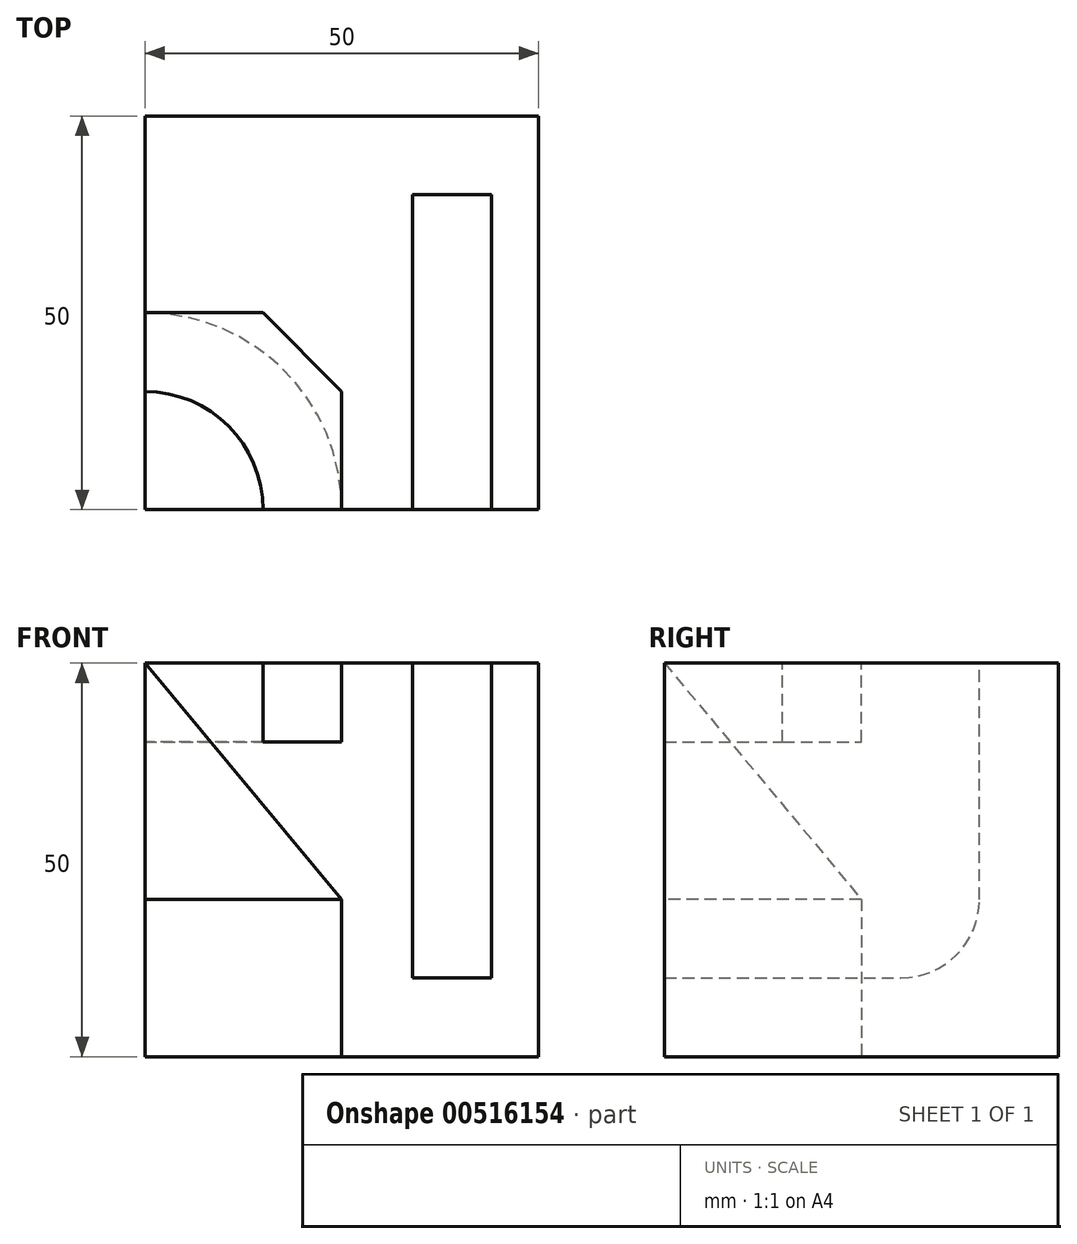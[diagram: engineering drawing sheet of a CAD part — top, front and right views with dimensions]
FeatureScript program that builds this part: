
annotation { "Feature Type Name" : "Feature", "Feature Type Description" : "" }
export const myFeature = defineFeature(function(context is Context, id is Id, definition is map)
    precondition{}
    {
        {
            var Q0;
            Q0=qCreatedBy(makeId("Top.planeOp"),FACE);
            var sketch = newSketch(context, id + "F0", { "sketchPlane" : qUnion([Q0])});
            skLineSegment(sketch, "E0.bottom", {"start": v(0, 0) * mm, "end": v(50, 0) * mm});
            skLineSegment(sketch, "E0.top", {"start": v(0, 50) * mm, "end": v(50, 50) * mm});
            skLineSegment(sketch, "E0.left", {"start": v(0, 0) * mm, "end": v(0, 50) * mm});
            skLineSegment(sketch, "E0.right", {"start": v(50, 0) * mm, "end": v(50, 50) * mm});
            skSolve(sketch);
        }
        {
            var Q0;
            Q0=makeQuery(id+"F0.imprint","IMPRINT",FACE,{"disambiguationData":[TD([[makeQuery(id+"F0.imprint","IMPRINT",EDGE,{"derivedFrom":sQuery(id+"F0.wireOp",EDGE,"E0.bottom")}),1.0]])]});
            extrude(context, id + "F1", {"entities" : qUnion([Q0]), "depth" : 50 * mm, "offsetDistance" : 25 * mm});
        }
        {
            var Q0;
            Q0=makeQuery(id+"F1.opExtrude","CAP_FACE",FACE,{"disambiguationData":[OSD([sQuery(id+"F0.wireOp",EDGE,"E0.bottom"),sQuery(id+"F0.wireOp",EDGE,"E0.top"),sQuery(id+"F0.wireOp",EDGE,"E0.left"),sQuery(id+"F0.wireOp",EDGE,"E0.right")])],"isStart":false});
            var sketch = newSketch(context, id + "F2", { "sketchPlane" : qUnion([Q0])});
            skCircle(sketch, "E1", {"center": v(0, 0) * mm, "radius": 15 * mm});
            skLineSegment(sketch, "E2.bottom", {"start": v(0, 0) * mm, "end": v(25, 0) * mm});
            skLineSegment(sketch, "E2.top", {"start": v(0, 25) * mm, "end": v(25, 25) * mm});
            skLineSegment(sketch, "E2.left", {"start": v(0, 0) * mm, "end": v(0, 25) * mm});
            skLineSegment(sketch, "E2.right", {"start": v(25, 0) * mm, "end": v(25, 25) * mm});
            skLineSegment(sketch, "E3", {"start": v(15, 25) * mm, "end": v(25, 15) * mm});
            skSolve(sketch);
        }
        {
            var Q0;
            {var subQ5=sQuery(id+"F2.wireOp",EDGE,"E3");Q0=makeQuery(id+"F2.imprint","IMPRINT",FACE,{"disambiguationData":[TD([[makeQuery(id+"F2.imprint","IMPRINT",EDGE,{"derivedFrom":subQ5}),-1.0]])]});}
            extrude(context, id + "F3", {"entities" : qUnion([Q0]), "operationType" : NewBodyOperationType.REMOVE, "oppositeDirection" : true, "depth" : 10 * mm, "offsetDistance" : 25 * mm});
        }
        {
            var Q0;
            {var subQ0=sQuery(id+"F0.wireOp",EDGE,"E0.left");var subQ1=sQuery(id+"F0.wireOp",EDGE,"E0.top");var subQ2=sQuery(id+"F0.wireOp",EDGE,"E0.right");var subQ3=sQuery(id+"F0.wireOp",EDGE,"E0.bottom");Q0=makeQuery(id+"F3.boolean.opBoolean","SPLIT",FACE,{"disambiguationData":[TD([makeQuery(id+"F1.opExtrude","SWEPT_FACE",FACE,{"disambiguationData":[OSD([subQ1])]})])],"derivedFrom":makeQuery(id+"F1.opExtrude","CAP_FACE",FACE,{"disambiguationData":[OSD([subQ3,subQ1,subQ0,subQ2])],"isStart":false})});}
            var sketch = newSketch(context, id + "F4", { "sketchPlane" : qUnion([Q0])});
            skLineSegment(sketch, "E4.bottom", {"start": v(34, 0) * mm, "end": v(44, 0) * mm});
            skLineSegment(sketch, "E4.top", {"start": v(34, 40) * mm, "end": v(44, 40) * mm});
            skLineSegment(sketch, "E4.left", {"start": v(34, 0) * mm, "end": v(34, 40) * mm});
            skLineSegment(sketch, "E4.right", {"start": v(44, 0) * mm, "end": v(44, 40) * mm});
            skSolve(sketch);
        }
        {
            var Q0;
            Q0=makeQuery(id+"F4.imprint","IMPRINT",FACE,{"disambiguationData":[TD([[makeQuery(id+"F4.imprint","IMPRINT",EDGE,{"derivedFrom":sQuery(id+"F4.wireOp",EDGE,"E4.bottom")}),1.0]])]});
            extrude(context, id + "F5", {"entities" : qUnion([Q0]), "operationType" : NewBodyOperationType.REMOVE, "oppositeDirection" : true, "depth" : 40 * mm, "offsetDistance" : 25 * mm});
        }
        {
            var Q0;
            Q0=makeQuery(id+"F5.boolean.opBoolean","COPY",EDGE,{"derivedFrom":makeQuery(id+"F5.opExtrude","CAP_EDGE",EDGE,{"disambiguationData":[OSD([sQuery(id+"F4.wireOp",EDGE,"E4.top")])],"isStart":false})});
            fillet(context, id + "F6", {"entities" : qUnion([Q0]), "radius" : 10 * mm, "tangentPropagation" : true, "allowEdgeOverflow" : false});
        }
        {
            var Q0;
            Q0=makeQuery(id+"F1.opExtrude","CAP_FACE",FACE,{"disambiguationData":[OSD([sQuery(id+"F0.wireOp",EDGE,"E0.bottom"),sQuery(id+"F0.wireOp",EDGE,"E0.top"),sQuery(id+"F0.wireOp",EDGE,"E0.left"),sQuery(id+"F0.wireOp",EDGE,"E0.right")])],"isStart":true});
            var sketch = newSketch(context, id + "F7", { "sketchPlane" : qUnion([Q0])});
            skCircle(sketch, "E5", {"center": v(0, 0) * mm, "radius": 25 * mm});
            skSolve(sketch);
        }
        {
            var Q0;
            {var subQ0=sQuery(id+"F7.wireOp",EDGE,"E5");var subQ1=makeQuery(id+"F1.opExtrude","CAP_EDGE",EDGE,{"disambiguationData":[OSD([sQuery(id+"F0.wireOp",EDGE,"E0.bottom")])],"isStart":true});var subQ2=makeQuery(id+"F7.imprint","INTERSECT",VERTEX,{"derivedFrom":[subQ1,subQ0]});Q0=makeQuery(id+"F7.imprint","IMPRINT",FACE,{"disambiguationData":[TD([[makeQuery(id+"F7.imprint","IMPRINT",EDGE,{"disambiguationData":[TD([[subQ2,1.0]])],"derivedFrom":subQ0}),1.0]])]});}
            extrude(context, id + "F8", {"entities" : qUnion([Q0]), "operationType" : NewBodyOperationType.REMOVE, "oppositeDirection" : true, "depth" : 20 * mm, "offsetDistance" : 25 * mm});
        }
        {
            var Q0;
            Q0=makeQuery(id+"F1.opExtrude","SWEPT_FACE",FACE,{"disambiguationData":[OSD([sQuery(id+"F0.wireOp",EDGE,"E0.bottom")])]});
            var sketch = newSketch(context, id + "F9", { "sketchPlane" : qUnion([Q0])});
            skLineSegment(sketch, "E6", {"start": v(25, 20) * mm, "end": v(0, 50) * mm});
            skSolve(sketch);
        }
        {
            var Q0;
            Q0=makeQuery(id+"F9.imprint","IMPRINT",FACE,{"disambiguationData":[TD([[makeQuery(id+"F9.imprint","IMPRINT",EDGE,{"derivedFrom":sQuery(id+"F9.wireOp",EDGE,"E6")}),1.0]])]});
            var Q1;
            Q1=makeQuery(id+"F8.boolean.opBoolean","COPY",FACE,{"derivedFrom":makeQuery(id+"F8.opExtrude","SWEPT_FACE",FACE,{"disambiguationData":[OSD([sQuery(id+"F7.wireOp",EDGE,"E5")])]})});
            revolve(context, id + "F10", {"operationType" : NewBodyOperationType.REMOVE, "entities" : qUnion([Q0]), "axis" : qUnion([Q1]), "revolveType" : RevolveType.FULL, "oppositeDirection" : true});
        }
    });
